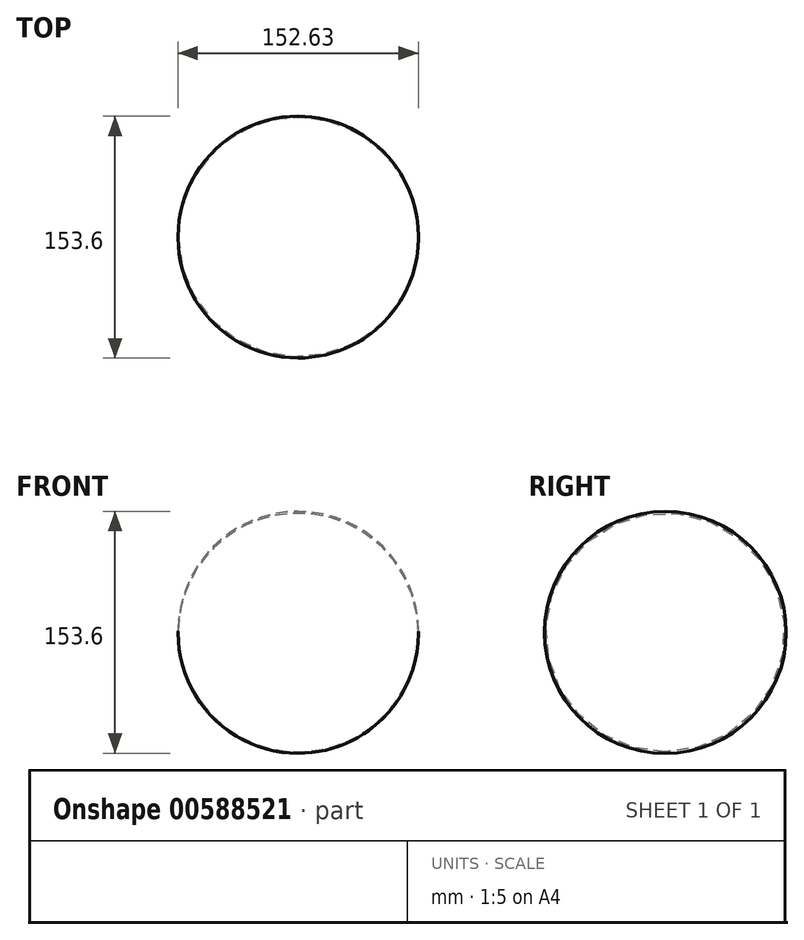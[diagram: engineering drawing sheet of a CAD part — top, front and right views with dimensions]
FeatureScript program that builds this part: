
annotation { "Feature Type Name" : "Feature", "Feature Type Description" : "" }
export const myFeature = defineFeature(function(context is Context, id is Id, definition is map)
    precondition{}
    {
        {
            var Q0;
            Q0=qCreatedBy(makeId("Top.planeOp"),FACE);
            var sketch = newSketch(context, id + "F0", { "sketchPlane" : qUnion([Q0])});
            skArc(sketch, "E0", {"start": v(-75.35, 0) * mm, "mid": v(0.96, -75.83) * mm, "end": v(77.27, 0) * mm});
            skLineSegment(sketch, "E1", {"start": v(-91.97, 0) * mm, "end": v(89.58, 0) * mm});
            skSolve(sketch);
        }
        {
            var Q0;
            {var subQ0=sQuery(id+"F0.wireOp",EDGE,"E0");Q0=makeQuery(id+"F0.imprint","IMPRINT",FACE,{"disambiguationData":[TD([[makeQuery(id+"F0.imprint","IMPRINT",EDGE,{"derivedFrom":subQ0}),1.0]])]});}
            var Q1;
            Q1=sQuery(id+"F0.wireOp",EDGE,"E1");
            revolve(context, id + "F1", {"entities" : qUnion([Q0]), "axis" : qUnion([Q1]), "revolveType" : RevolveType.FULL});
        }
        {
            var Q0;
            Q0=qCreatedBy(makeId("Front.planeOp"),FACE);
            var sketch = newSketch(context, id + "F2", { "sketchPlane" : qUnion([Q0])});
            skCircle(sketch, "E2", {"center": v(0, 0) * mm, "radius": 28.83 * mm});
            skSolve(sketch);
        }
        {
            var Q0;
            Q0 = qSketchRegion(id + "F2", true);
            extrude(context, id + "F3", {"entities" : qUnion([Q0]), "operationType" : NewBodyOperationType.ADD, "depth" : 68.6 * mm, "offsetDistance" : 25 * mm});
        }
    });
